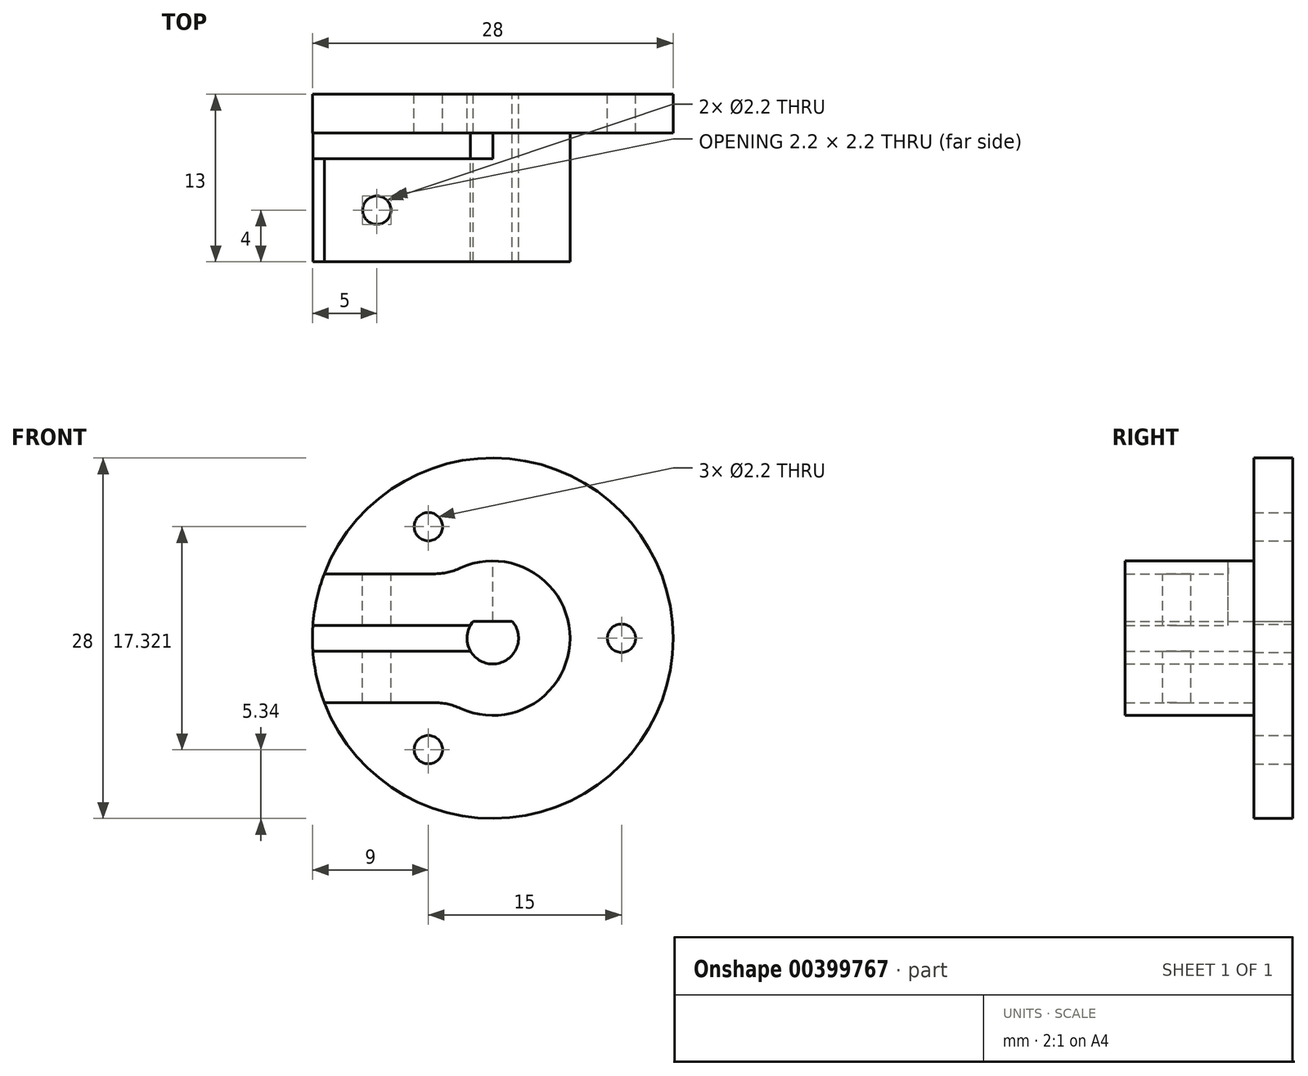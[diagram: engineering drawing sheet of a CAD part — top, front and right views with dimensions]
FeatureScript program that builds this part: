
annotation { "Feature Type Name" : "Feature", "Feature Type Description" : "" }
export const myFeature = defineFeature(function(context is Context, id is Id, definition is map)
    precondition{}
    {
        {
            var Q0;
            Q0=qCreatedBy(makeId("Front.planeOp"),FACE);
            var sketch = newSketch(context, id + "F0", { "sketchPlane" : qUnion([Q0])});
            skCircle(sketch, "E0", {"center": v(0, 0) * mm, "radius": 14 * mm});
            skCircle(sketch, "E1.cCircle", {"center": v(0, 0) * mm, "radius": 10 * mm, "construction": true});
            skLineSegment(sketch, "E1.0", {"start": v(10, 0) * mm, "end": v(-5, -8.66) * mm, "construction": true});
            skLineSegment(sketch, "E1.1", {"start": v(-5, -8.66) * mm, "end": v(-5, 8.66) * mm, "construction": true});
            skLineSegment(sketch, "E1.2", {"start": v(-5, 8.66) * mm, "end": v(10, 0) * mm, "construction": true});
            skPoint(sketch, "E2", {"position": v(-5, 8.66) * mm});
            skPoint(sketch, "E3", {"position": v(-5, -8.66) * mm});
            skPoint(sketch, "E4", {"position": v(10, 0) * mm});
            skCircle(sketch, "E5", {"center": v(-5, 8.66) * mm, "radius": 1.1 * mm});
            skCircle(sketch, "E6", {"center": v(-5, -8.66) * mm, "radius": 1.1 * mm});
            skCircle(sketch, "E7", {"center": v(10, 0) * mm, "radius": 1.1 * mm});
            skSolve(sketch);
        }
        {
            var Q0;
            Q0=makeQuery(id+"F0.imprint","IMPRINT",FACE,{"disambiguationData":[TD([[makeQuery(id+"F0.imprint","IMPRINT",EDGE,{"derivedFrom":sQuery(id+"F0.wireOp",EDGE,"7shuBnMs-Iyvi-q2Ir-Qhl9-R8Q4JHfXM2dq")}),-1.0]])]});
            var Q1;
            Q1=makeQuery(id+"F0.imprint","IMPRINT",FACE,{"disambiguationData":[TD([[makeQuery(id+"F0.imprint","IMPRINT",EDGE,{"derivedFrom":sQuery(id+"F0.wireOp",EDGE,"E0")}),1.0]])]});
            extrude(context, id + "F1", {"entities" : qUnion([Q0, Q1]), "depth" : 3 * mm, "offsetDistance" : 25 * mm});
        }
        {
            var Q0;
            Q0=makeQuery(id+"F1.opExtrude","CAP_FACE",FACE,{"disambiguationData":[OSD([sQuery(id+"F0.wireOp",EDGE,"7shuBnMs-Iyvi-q2Ir-Qhl9-R8Q4JHfXM2dq"),sQuery(id+"F0.wireOp",EDGE,"tOBiGZAK-7TtL-BwBf-j3e8-1F4MY2KjswT6"),sQuery(id+"F0.wireOp",EDGE,"pEEXO6KY-tjO8-xeXR-OTIJ-kHnvypdrCYqa"),sQuery(id+"F0.wireOp",EDGE,"E0")])],"isStart":false});
            var sketch = newSketch(context, id + "F2", { "sketchPlane" : qUnion([Q0])});
            skArc(sketch, "E8", {"start": v(0, -6) * mm, "mid": v(6, 0) * mm, "end": v(0, 6) * mm});
            skPoint(sketch, "E9", {"position": v(0, 6) * mm});
            skPoint(sketch, "E10", {"position": v(0, -6) * mm});
            skPoint(sketch, "E11", {"position": v(-12.65, 6) * mm});
            skPoint(sketch, "E12", {"position": v(-12.65, -6) * mm});
            skArc(sketch, "E13", {"start": v(-3.32, -5) * mm, "mid": v(6, 0) * mm, "end": v(-3.32, 5) * mm});
            skPoint(sketch, "E14", {"position": v(-3.32, 5) * mm});
            skPoint(sketch, "E15", {"position": v(-3.32, -5) * mm});
            skLineSegment(sketch, "E16.bottom", {"start": v(-3.32, -5) * mm, "end": v(-13.08, -5) * mm});
            skLineSegment(sketch, "E16.top", {"start": v(-3.32, 5) * mm, "end": v(-13.08, 5) * mm});
            skPoint(sketch, "E17", {"position": v(-13.08, 5) * mm});
            skPoint(sketch, "E18", {"position": v(-13.08, -5) * mm});
            skArc(sketch, "E19", {"start": v(-13.08, 5) * mm, "mid": v(-14, 0) * mm, "end": v(-13.08, -5) * mm});
            skPoint(sketch, "E16.right.end.orphan", {"position": v(-16.3, 5) * mm});
            skSolve(sketch);
        }
        {
            var Q0;
            Q0=qSketchRegion(id+"F2",true);
            var Q1;
            Q1=makeQuery(id+"F2.imprint","IMPRINT",FACE,{"disambiguationData":[TD([[makeQuery(id+"F2.imprint","IMPRINT",EDGE,{"derivedFrom":sQuery(id+"F2.wireOp",EDGE,"E8")}),1.0]])]});
            extrude(context, id + "F3", {"entities" : qUnion([Q0, Q1]), "operationType" : NewBodyOperationType.ADD, "depth" : 10 * mm, "offsetDistance" : 25 * mm});
        }
        {
            var Q0;
            Q0=makeQuery(id+"F1.opExtrude","CAP_FACE",FACE,{"disambiguationData":[OSD([sQuery(id+"F0.wireOp",EDGE,"E0"),sQuery(id+"F0.wireOp",EDGE,"E5"),sQuery(id+"F0.wireOp",EDGE,"E6"),sQuery(id+"F0.wireOp",EDGE,"E7")])],"isStart":true});
            var sketch = newSketch(context, id + "F4", { "sketchPlane" : qUnion([Q0])});
            skArc(sketch, "E20", {"start": v(-1.5, 1.32) * mm, "mid": v(0, -2) * mm, "end": v(1.5, 1.32) * mm});
            skLineSegment(sketch, "E21.bottom", {"start": v(-1.5, 1.32) * mm, "end": v(1.5, 1.32) * mm});
            skPoint(sketch, "E21.top.start.orphan", {"position": v(-1.5, -1.32) * mm});
            skPoint(sketch, "E21.right.end.orphan", {"position": v(1.5, -1.32) * mm});
            skSolve(sketch);
        }
        {
            var Q0;
            Q0=qSketchRegion(id+"F4",true);
            extrude(context, id + "F5", {"entities" : qUnion([Q0]), "operationType" : NewBodyOperationType.REMOVE, "endBound" : BoundingType.THROUGH_ALL, "oppositeDirection" : true, "depth" : 25 * mm});
        }
        {
            var Q0;
            Q0=makeQuery(id+"F3.opExtrude","SWEPT_FACE",FACE,{"disambiguationData":[OSD([sQuery(id+"F2.wireOp",EDGE,"E16.top")])]});
            var sketch = newSketch(context, id + "F6", { "sketchPlane" : qUnion([Q0])});
            skLineSegment(sketch, "E22.bottom", {"start": v(0, -3) * mm, "end": v(-14, -3) * mm});
            skLineSegment(sketch, "E22.top", {"start": v(0, -5) * mm, "end": v(-14, -5) * mm});
            skLineSegment(sketch, "E22.left", {"start": v(0, -3) * mm, "end": v(0, -5) * mm});
            skLineSegment(sketch, "E22.right", {"start": v(-14, -3) * mm, "end": v(-14, -5) * mm});
            skSolve(sketch);
        }
        {
            var Q0;
            Q0 = qSketchRegion(id + "F6", true);
            extrude(context, id + "F7", {"entities" : qUnion([Q0]), "operationType" : NewBodyOperationType.REMOVE, "endBound" : BoundingType.SYMMETRIC, "oppositeDirection" : true, "depth" : 12 * mm, "offsetDistance" : 25 * mm});
        }
        {
            var Q0;
            Q0=makeQuery(id+"F3.opExtrude","CAP_FACE",FACE,{"disambiguationData":[OSD([sQuery(id+"F2.wireOp",EDGE,"E13"),sQuery(id+"F2.wireOp",EDGE,"E16.bottom"),sQuery(id+"F2.wireOp",EDGE,"E16.top"),sQuery(id+"F2.wireOp",EDGE,"E19")])],"isStart":false});
            var sketch = newSketch(context, id + "F8", { "sketchPlane" : qUnion([Q0])});
            skLineSegment(sketch, "E23.bottom", {"start": v(-14, -1) * mm, "end": v(0, -1) * mm});
            skLineSegment(sketch, "E23.top", {"start": v(-14, 1) * mm, "end": v(0, 1) * mm});
            skLineSegment(sketch, "E23.left", {"start": v(-14, -1) * mm, "end": v(-14, 1) * mm});
            skPoint(sketch, "E23.middle", {"position": v(0, 0) * mm});
            skLineSegment(sketch, "E24", {"start": v(0, 1) * mm, "end": v(0, -1) * mm});
            skPoint(sketch, "E23.right.end.orphan", {"position": v(14, 1) * mm});
            skPoint(sketch, "E23.right.start.orphan", {"position": v(14, -1) * mm});
            skSolve(sketch);
        }
        {
            var Q0;
            Q0 = qSketchRegion(id + "F8", true);
            extrude(context, id + "F9", {"entities" : qUnion([Q0]), "operationType" : NewBodyOperationType.REMOVE, "oppositeDirection" : true, "depth" : 8 * mm, "offsetDistance" : 25 * mm});
        }
        {
            var Q0;
            Q0=makeQuery(id+"F7.boolean.opBoolean","MERGE",FACE,{"derivedFrom":[makeQuery(id+"F1.opExtrude","CAP_FACE",FACE,{"disambiguationData":[OSD([sQuery(id+"F0.wireOp",EDGE,"E0"),sQuery(id+"F0.wireOp",EDGE,"E5"),sQuery(id+"F0.wireOp",EDGE,"E6"),sQuery(id+"F0.wireOp",EDGE,"E7")])],"isStart":false}),makeQuery(id+"F7.opExtrude","SWEPT_FACE",FACE,{"disambiguationData":[OSD([sQuery(id+"F6.wireOp",EDGE,"E22.bottom")])]})]});
            var sketch = newSketch(context, id + "F10", { "sketchPlane" : qUnion([Q0])});
            skCircle(sketch, "E25", {"center": v(-5, 8.66) * mm, "radius": 3 * mm});
            skSolve(sketch);
        }
        {
            var Q0;
            Q0 = qSketchRegion(id + "F10", true);
            extrude(context, id + "F11", {"entities" : qUnion([Q0]), "operationType" : NewBodyOperationType.REMOVE, "depth" : 10 * mm, "offsetDistance" : 25 * mm});
        }
        {
            var Q0;
            Q0=makeQuery(id+"F3.opExtrude","SWEPT_EDGE",EDGE,{"disambiguationData":[OSD([sQuery(id+"F2.wireOp",EDGE,"E13"),sQuery(id+"F2.wireOp",EDGE,"E16.top")])]});
            fillet(context, id + "F12", {"entities" : qUnion([Q0]), "radius" : 5 * mm, "tangentPropagation" : true, "allowEdgeOverflow" : false});
        }
        {
            var Q0;
            Q0=makeQuery(id+"F3.opExtrude","SWEPT_EDGE",EDGE,{"disambiguationData":[OSD([sQuery(id+"F2.wireOp",EDGE,"E13"),sQuery(id+"F2.wireOp",EDGE,"E16.bottom")])]});
            fillet(context, id + "F13", {"entities" : qUnion([Q0]), "radius" : 5 * mm, "tangentPropagation" : true, "allowEdgeOverflow" : false});
        }
        {
            var Q0;
            Q0=makeQuery(id+"F3.opExtrude","SWEPT_FACE",FACE,{"disambiguationData":[OSD([sQuery(id+"F2.wireOp",EDGE,"E16.top")])]});
            var sketch = newSketch(context, id + "F14", { "sketchPlane" : qUnion([Q0])});
            skCircle(sketch, "E26", {"center": v(-9, -9) * mm, "radius": 1.1 * mm});
            skSolve(sketch);
        }
        {
            var Q0;
            Q0 = qSketchRegion(id + "F14", true);
            extrude(context, id + "F15", {"entities" : qUnion([Q0]), "operationType" : NewBodyOperationType.REMOVE, "endBound" : BoundingType.THROUGH_ALL, "oppositeDirection" : true, "depth" : 25 * mm, "offsetDistance" : 25 * mm});
        }
    });
